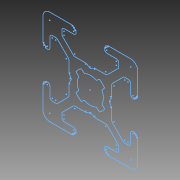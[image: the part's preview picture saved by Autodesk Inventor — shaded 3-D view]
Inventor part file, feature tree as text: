
AUTODESK INVENTOR PART (.ipt)
format: ipt  version: 2011 (Build 150239000, 239)  size: 110,080 bytes
history: native  units: in
note: dims shown in document units (in); Inventor stores cm internally (conversion verified against a paired STEP export)
features: sketch x1
ambient origin geometry x8: Origin, YZ Plane, XZ Plane, XY Plane, X Axis, Y Axis, Z Axis, Center Point
feature tree (1):
  sketch  "Sketch1"
